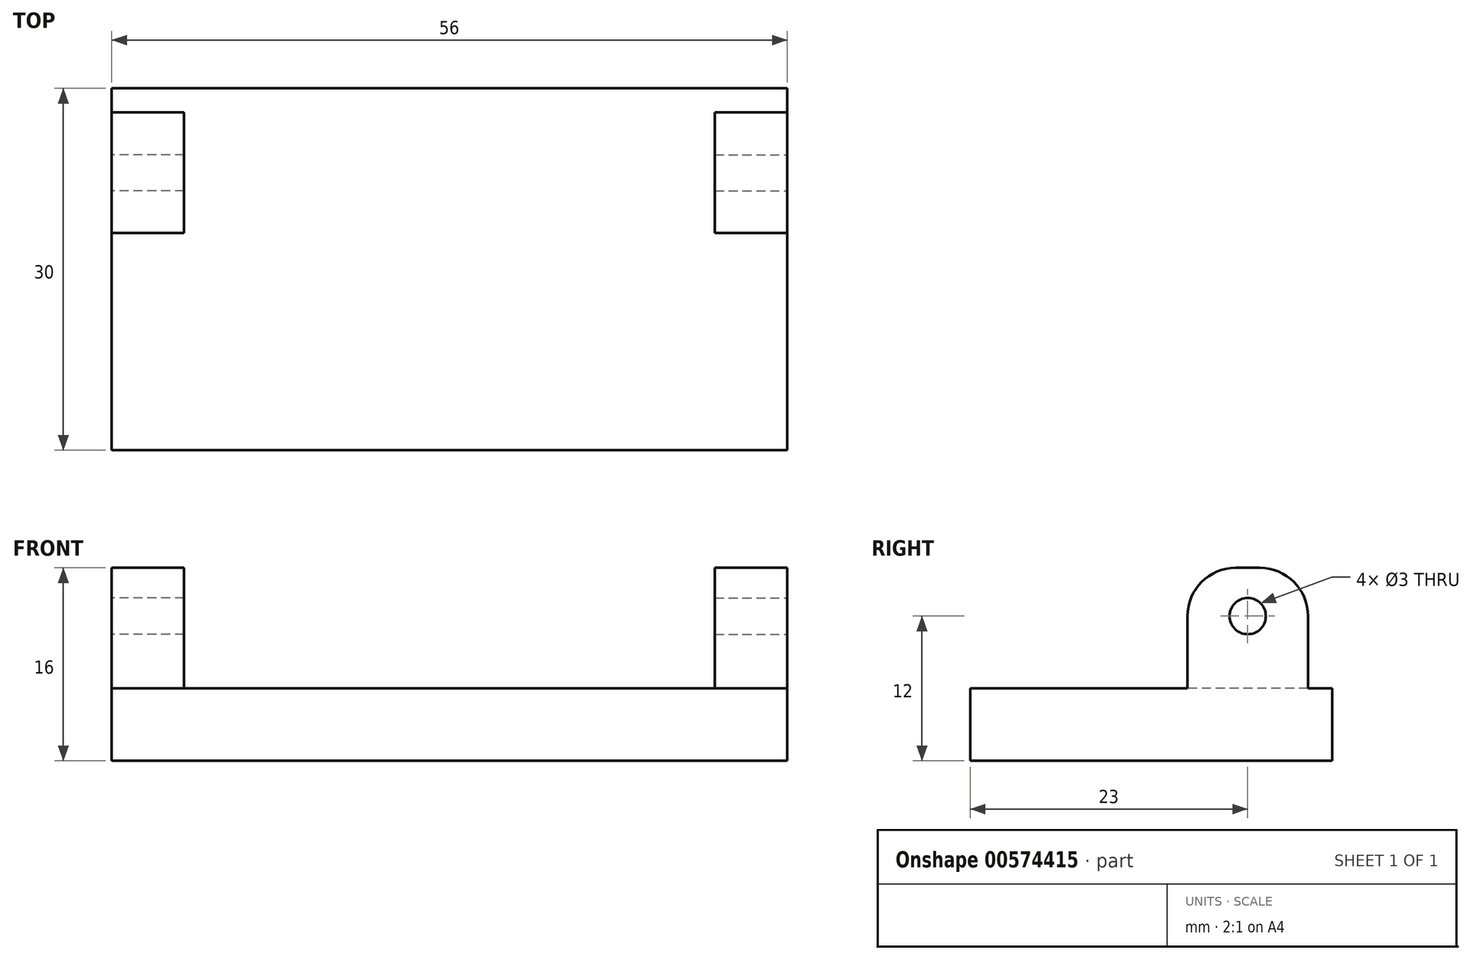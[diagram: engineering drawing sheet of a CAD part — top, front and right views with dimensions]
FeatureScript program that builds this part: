
annotation { "Feature Type Name" : "Feature", "Feature Type Description" : "" }
export const myFeature = defineFeature(function(context is Context, id is Id, definition is map)
    precondition{}
    {
        {
            var Q0;
            Q0=qCreatedBy(makeId("Top.planeOp"),FACE);
            var sketch = newSketch(context, id + "F0", { "sketchPlane" : qUnion([Q0])});
            skLineSegment(sketch, "E0.bottom", {"start": v(0, -15) * mm, "end": v(28, -15) * mm});
            skLineSegment(sketch, "E0.top", {"start": v(0, 15) * mm, "end": v(28, 15) * mm});
            skLineSegment(sketch, "E0.left", {"start": v(0, -15) * mm, "end": v(0, 15) * mm});
            skLineSegment(sketch, "E0.right", {"start": v(28, -15) * mm, "end": v(28, 15) * mm});
            skSolve(sketch);
        }
        {
            var Q0;
            Q0 = qSketchRegion(id + "F0", true);
            extrude(context, id + "F1", {"entities" : qUnion([Q0]), "depth" : 6 * mm, "offsetDistance" : 25 * mm});
        }
        {
            var Q0;
            Q0=makeQuery(id+"F1.opExtrude","CAP_FACE",FACE,{"disambiguationData":[OSD([sQuery(id+"F0.wireOp",EDGE,"E0.bottom"),sQuery(id+"F0.wireOp",EDGE,"E0.top"),sQuery(id+"F0.wireOp",EDGE,"E0.left"),sQuery(id+"F0.wireOp",EDGE,"E0.right")])],"isStart":false});
            var sketch = newSketch(context, id + "F2", { "sketchPlane" : qUnion([Q0])});
            skLineSegment(sketch, "E1.bottom", {"start": v(22, 13) * mm, "end": v(28, 13) * mm});
            skLineSegment(sketch, "E1.top", {"start": v(22, 3) * mm, "end": v(28, 3) * mm});
            skLineSegment(sketch, "E1.left", {"start": v(22, 13) * mm, "end": v(22, 3) * mm});
            skLineSegment(sketch, "E1.right", {"start": v(28, 13) * mm, "end": v(28, 3) * mm});
            skSolve(sketch);
        }
        {
            var Q0;
            Q0 = qSketchRegion(id + "F2", true);
            extrude(context, id + "F3", {"entities" : qUnion([Q0]), "operationType" : NewBodyOperationType.ADD, "depth" : 10 * mm, "offsetDistance" : 25 * mm});
        }
        {
            var Q0;
            Q0=makeQuery(id+"F3.opExtrude","CAP_EDGE",EDGE,{"disambiguationData":[OSD([sQuery(id+"F2.wireOp",EDGE,"E1.top")])],"isStart":false});
            var Q1;
            Q1=makeQuery(id+"F3.opExtrude","CAP_EDGE",EDGE,{"disambiguationData":[OSD([sQuery(id+"F2.wireOp",EDGE,"E1.bottom")])],"isStart":false});
            fillet(context, id + "F4", {"entities" : qUnion([Q0, Q1]), "radius" : 4 * mm, "tangentPropagation" : true, "allowEdgeOverflow" : false});
        }
        {
            var Q0;
            Q0=makeQuery(id+"F3.boolean.opBoolean","MERGE",FACE,{"derivedFrom":[makeQuery(id+"F1.opExtrude","SWEPT_FACE",FACE,{"disambiguationData":[OSD([sQuery(id+"F0.wireOp",EDGE,"E0.right")])]}),makeQuery(id+"F3.opExtrude","SWEPT_FACE",FACE,{"disambiguationData":[OSD([sQuery(id+"F2.wireOp",EDGE,"E1.right")])]})]});
            var sketch = newSketch(context, id + "F5", { "sketchPlane" : qUnion([Q0])});
            skCircle(sketch, "E2", {"center": v(8, 12) * mm, "radius": 1.5 * mm});
            skPoint(sketch, "E2.centerSnap0", {"position": v(8, 16) * mm});
            skSolve(sketch);
        }
        {
            var Q0;
            Q0 = qSketchRegion(id + "F5", true);
            extrude(context, id + "F6", {"entities" : qUnion([Q0]), "operationType" : NewBodyOperationType.REMOVE, "endBound" : BoundingType.THROUGH_ALL, "oppositeDirection" : true, "depth" : 6 * mm, "offsetDistance" : 25 * mm});
        }
        {
            var Q0;
            Q0=makeQuery(id+"F1.opExtrude","SWEPT_BODY",BODY,{"disambiguationData":[OSD([sQuery(id+"F0.wireOp",EDGE,"E0.bottom"),sQuery(id+"F0.wireOp",EDGE,"E0.top"),sQuery(id+"F0.wireOp",EDGE,"E0.left"),sQuery(id+"F0.wireOp",EDGE,"E0.right")])]});
            var Q1;
            Q1=makeQuery(id+"F1.opExtrude","SWEPT_FACE",FACE,{"disambiguationData":[OSD([sQuery(id+"F0.wireOp",EDGE,"E0.left")])]});
            mirror(context, id + "F7", {"operationType" : NewBodyOperationType.ADD, "entities" : qUnion([Q0]), "mirrorPlane" : qUnion([Q1])});
        }
        {
            var Q0;
            Q0=makeQuery(id+"F1.opExtrude","SWEPT_BODY",BODY,{"disambiguationData":[OSD([sQuery(id+"F0.wireOp",EDGE,"E0.bottom"),sQuery(id+"F0.wireOp",EDGE,"E0.top"),sQuery(id+"F0.wireOp",EDGE,"E0.left"),sQuery(id+"F0.wireOp",EDGE,"E0.right")])]});
            transform(context, id + "F8", {"entities" : qUnion([Q0]), "transformType" : TransformType.TRANSLATION_3D, "dx" : 0 * mm, "dy" : 0 * mm, "dz" : 0 * mm, "makeCopy" : true});
        }
    });
